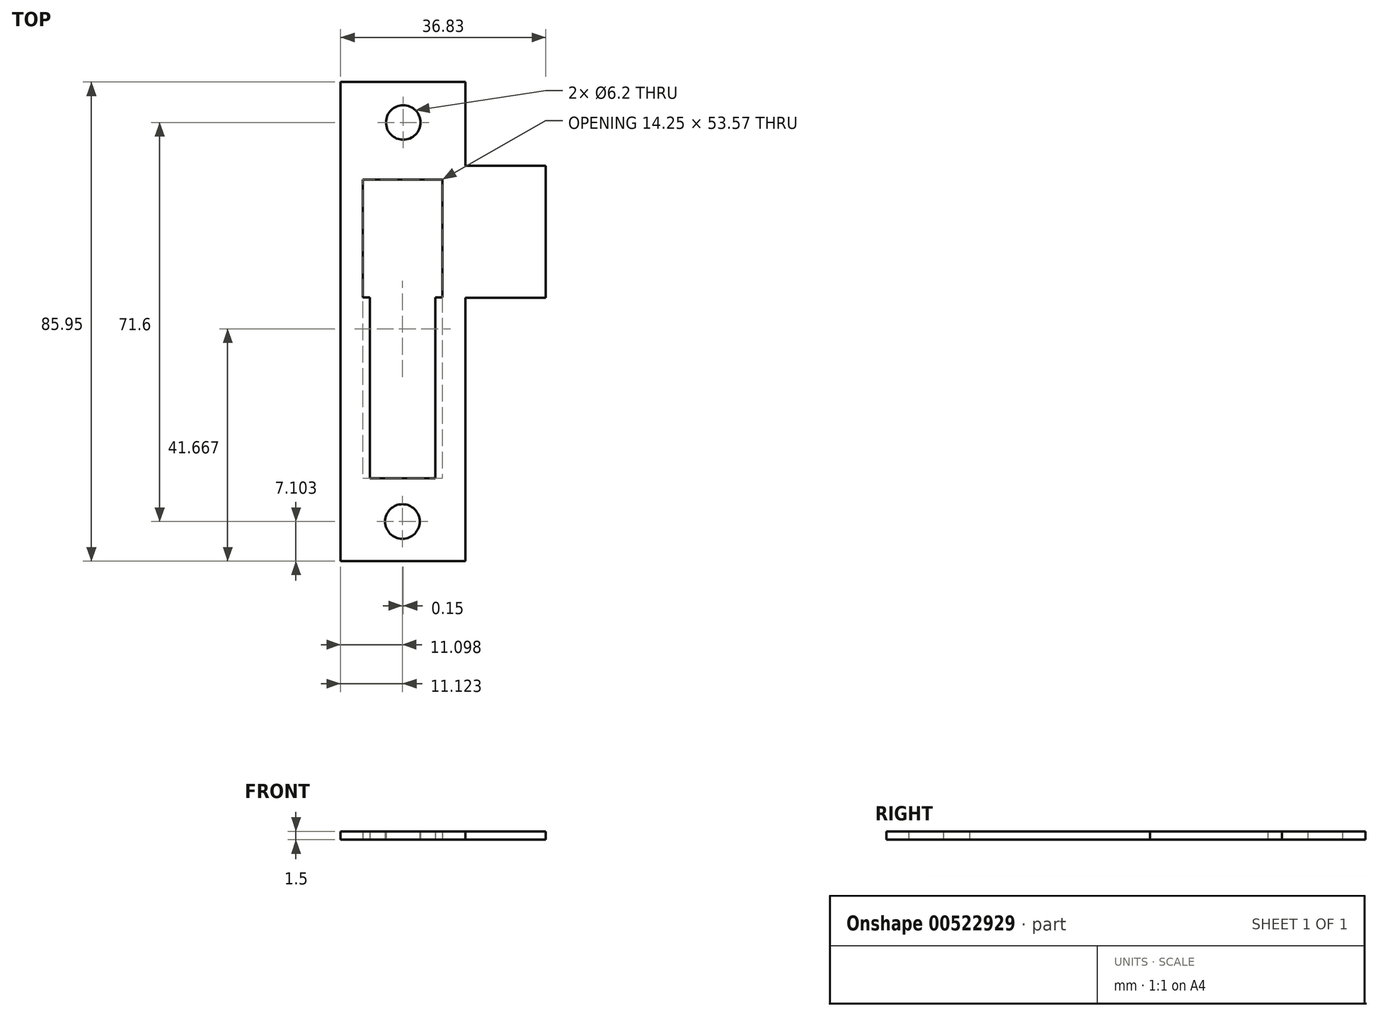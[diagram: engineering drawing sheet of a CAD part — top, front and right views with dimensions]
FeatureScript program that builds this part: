
annotation { "Feature Type Name" : "Feature", "Feature Type Description" : "" }
export const myFeature = defineFeature(function(context is Context, id is Id, definition is map)
    precondition{}
    {
        {
            var Q0;
            Q0=qCreatedBy(makeId("Top.planeOp"),FACE);
            var sketch = newSketch(context, id + "F0", { "sketchPlane" : qUnion([Q0])});
            skLineSegment(sketch, "E0", {"start": v(-33.84, 36.81) * mm, "end": v(-33.84, -49.14) * mm});
            skLineSegment(sketch, "E1", {"start": v(-33.84, -49.14) * mm, "end": v(-11.46, -49.14) * mm});
            skLineSegment(sketch, "E2", {"start": v(-11.46, -49.14) * mm, "end": v(-11.46, -1.89) * mm});
            skLineSegment(sketch, "E3", {"start": v(-11.46, -1.89) * mm, "end": v(2.99, -1.89) * mm});
            skLineSegment(sketch, "E4", {"start": v(2.99, -1.89) * mm, "end": v(2.99, 21.81) * mm});
            skLineSegment(sketch, "E5", {"start": v(2.99, 21.81) * mm, "end": v(-11.46, 21.81) * mm});
            skLineSegment(sketch, "E6", {"start": v(-11.46, 21.81) * mm, "end": v(-11.46, 36.81) * mm});
            skLineSegment(sketch, "E7", {"start": v(-11.46, 36.81) * mm, "end": v(-33.84, 36.81) * mm});
            skSolve(sketch);
        }
        {
            var Q0;
            Q0=makeQuery(id+"F0.imprint","IMPRINT",FACE,{"disambiguationData":[TD([[makeQuery(id+"F0.imprint","IMPRINT",EDGE,{"derivedFrom":sQuery(id+"F0.wireOp",EDGE,"E0")}),1.0]])]});
            extrude(context, id + "F1", {"entities" : qUnion([Q0]), "depth" : 1.5 * mm, "offsetDistance" : 25 * mm});
        }
        {
            var Q0;
            Q0=qCreatedBy(makeId("Top.planeOp"),FACE);
            var sketch = newSketch(context, id + "F2", { "sketchPlane" : qUnion([Q0])});
            skLineSegment(sketch, "E8", {"start": v(-29.84, 19.31) * mm, "end": v(-29.84, -1.84) * mm});
            skLineSegment(sketch, "E9", {"start": v(-29.84, -1.84) * mm, "end": v(-28.6, -1.84) * mm});
            skLineSegment(sketch, "E10", {"start": v(-28.6, -1.84) * mm, "end": v(-28.6, -34.26) * mm});
            skLineSegment(sketch, "E11", {"start": v(-28.6, -34.26) * mm, "end": v(-16.84, -34.26) * mm});
            skLineSegment(sketch, "E12", {"start": v(-16.84, -34.26) * mm, "end": v(-16.84, -1.84) * mm});
            skLineSegment(sketch, "E13", {"start": v(-16.84, -1.84) * mm, "end": v(-15.6, -1.84) * mm});
            skLineSegment(sketch, "E14", {"start": v(-15.6, -1.84) * mm, "end": v(-15.6, 19.31) * mm});
            skLineSegment(sketch, "E15", {"start": v(-15.6, 19.31) * mm, "end": v(-29.84, 19.31) * mm});
            skCircle(sketch, "E16", {"center": v(-22.6, 29.56) * mm, "radius": 3.1 * mm});
            skCircle(sketch, "E17", {"center": v(-22.74, -42.04) * mm, "radius": 3.1 * mm});
            skSolve(sketch);
        }
        {
            var Q0;
            Q0=makeQuery(id+"F2.imprint","IMPRINT",FACE,{"disambiguationData":[TD([[makeQuery(id+"F2.imprint","IMPRINT",EDGE,{"derivedFrom":sQuery(id+"F2.wireOp",EDGE,"E8")}),1.0]])]});
            var Q1;
            Q1=makeQuery(id+"F2.imprint","IMPRINT",FACE,{"disambiguationData":[TD([[makeQuery(id+"F2.imprint","IMPRINT",EDGE,{"derivedFrom":sQuery(id+"F2.wireOp",EDGE,"E17")}),1.0]])]});
            var Q2;
            Q2=makeQuery(id+"F2.imprint","IMPRINT",FACE,{"disambiguationData":[TD([[makeQuery(id+"F2.imprint","IMPRINT",EDGE,{"derivedFrom":sQuery(id+"F2.wireOp",EDGE,"E16")}),1.0]])]});
            extrude(context, id + "F3", {"entities" : qUnion([Q0, Q1, Q2]), "operationType" : NewBodyOperationType.REMOVE, "endBound" : BoundingType.THROUGH_ALL, "depth" : 25 * mm, "offsetDistance" : 25 * mm});
        }
    });
